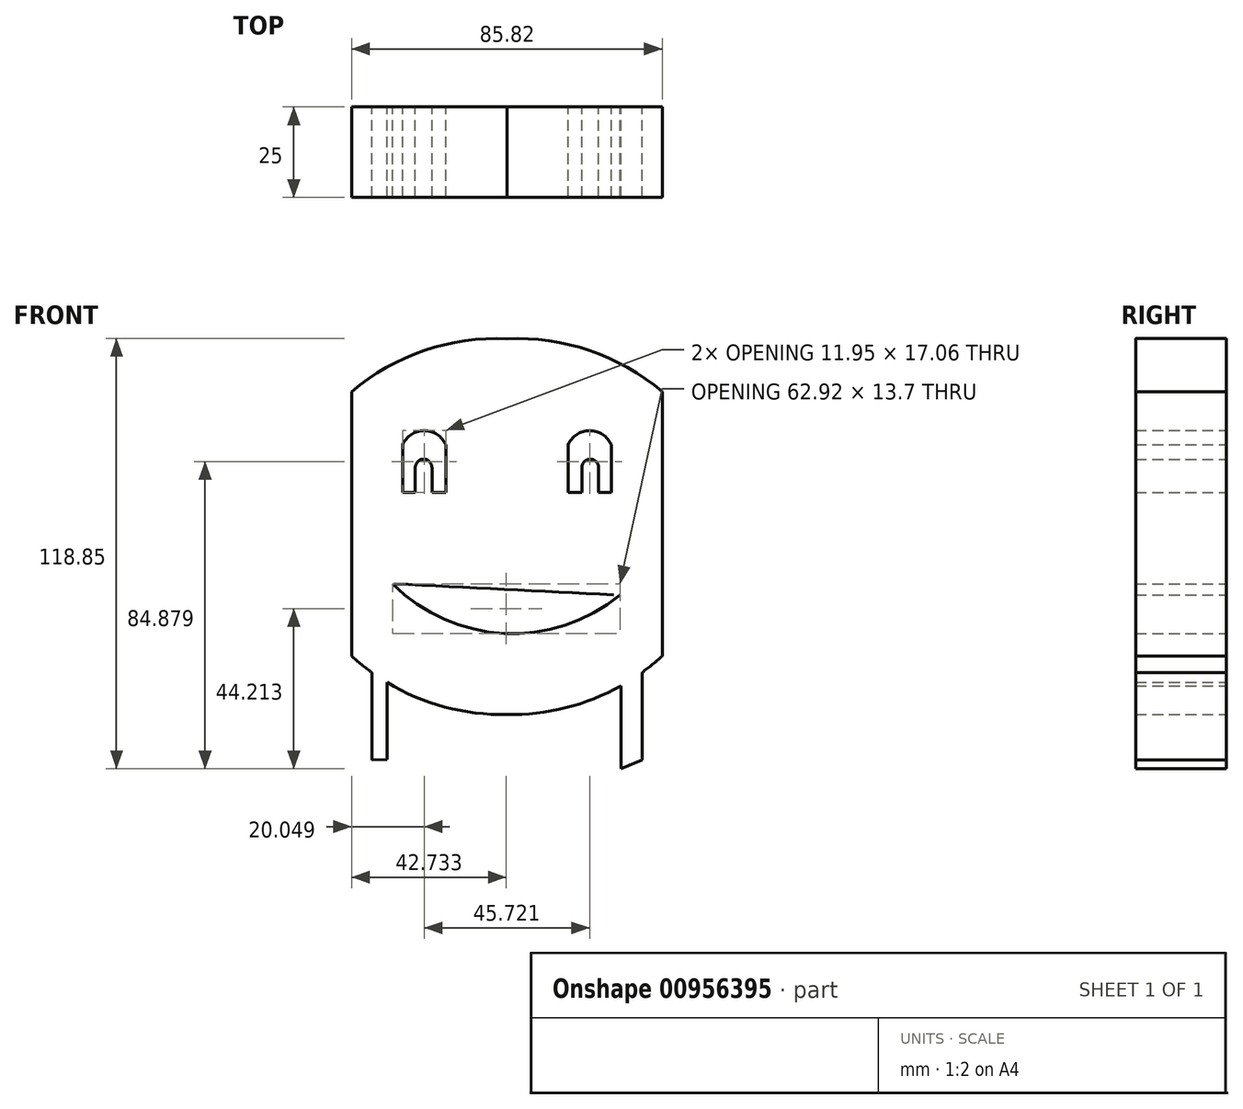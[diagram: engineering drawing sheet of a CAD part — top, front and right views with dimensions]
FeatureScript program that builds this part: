
annotation { "Feature Type Name" : "Feature", "Feature Type Description" : "" }
export const myFeature = defineFeature(function(context is Context, id is Id, definition is map)
    precondition{}
    {
        {
            var Q0;
            Q0=qCreatedBy(makeId("Front.planeOp"),FACE);
            var sketch = newSketch(context, id + "F0", { "sketchPlane" : qUnion([Q0])});
            skPoint(sketch, "E0", {"position": v(0, 0) * mm});
            skLineSegment(sketch, "E1", {"start": v(-37.34, -62.19) * mm, "end": v(-48.84, -66.36) * mm});
            skLineSegment(sketch, "E2", {"start": v(-37.34, -62.19) * mm, "end": v(-37.34, -67.06) * mm});
            skLineSegment(sketch, "E3", {"start": v(-37.34, -62.19) * mm, "end": v(-25.64, -67.08) * mm});
            skLineSegment(sketch, "E4.MirrorCS", {"start": v(37.34, -62.19) * mm, "end": v(25.64, -67.08) * mm});
            skLineSegment(sketch, "E5.MirrorCS", {"start": v(37.34, -62.19) * mm, "end": v(48.84, -66.36) * mm});
            skLineSegment(sketch, "E6.MirrorCS", {"start": v(37.34, -62.19) * mm, "end": v(37.34, -67.06) * mm});
            skArc(sketch, "E7", {"start": v(0, 54.16) * mm, "mid": v(-22.84, 50.9) * mm, "end": v(-42.91, 39.54) * mm});
            skLineSegment(sketch, "E8", {"start": v(-42.91, 39.54) * mm, "end": v(-42.91, -33.53) * mm});
            skArc(sketch, "E9", {"start": v(-42.91, -33.53) * mm, "mid": v(-23, -45.7) * mm, "end": v(0, -49.66) * mm});
            skLineSegment(sketch, "E10", {"start": v(-37.34, -62.19) * mm, "end": v(-37.34, -38.04) * mm});
            skLineSegment(sketch, "E11.MirrorCS", {"start": v(37.34, -62.19) * mm, "end": v(37.34, -38.04) * mm});
            skArc(sketch, "E12.MirrorCS", {"start": v(42.91, -33.53) * mm, "mid": v(23, -45.7) * mm, "end": v(0, -49.66) * mm});
            skLineSegment(sketch, "E13.MirrorCS", {"start": v(42.91, 39.54) * mm, "end": v(42.91, -33.53) * mm});
            skArc(sketch, "E14.MirrorCS", {"start": v(0, 54.16) * mm, "mid": v(22.84, 50.9) * mm, "end": v(42.91, 39.54) * mm});
            skLineSegment(sketch, "E15", {"start": v(-28.84, 11.73) * mm, "end": v(-16.88, 11.73) * mm});
            skLineSegment(sketch, "E16", {"start": v(-28.84, 11.73) * mm, "end": v(-28.84, 24.86) * mm});
            skLineSegment(sketch, "E17", {"start": v(-16.88, 11.73) * mm, "end": v(-16.88, 24.86) * mm});
            skArc(sketch, "E18", {"start": v(-16.88, 24.86) * mm, "mid": v(-22.86, 28.79) * mm, "end": v(-28.84, 24.86) * mm});
            skLineSegment(sketch, "E19.MirrorCS", {"start": v(16.88, 11.73) * mm, "end": v(16.88, 24.86) * mm});
            skArc(sketch, "E20.MirrorCS", {"start": v(16.88, 24.86) * mm, "mid": v(22.86, 28.79) * mm, "end": v(28.84, 24.86) * mm});
            skLineSegment(sketch, "E21.MirrorCS", {"start": v(28.84, 11.73) * mm, "end": v(28.84, 24.86) * mm});
            skLineSegment(sketch, "E22.MirrorCS", {"start": v(28.84, 11.73) * mm, "end": v(16.88, 11.73) * mm});
            skLineSegment(sketch, "E23", {"start": v(-25.3, 11.73) * mm, "end": v(-25.3, 18.59) * mm});
            skLineSegment(sketch, "E24", {"start": v(-20.71, 11.73) * mm, "end": v(-20.71, 18.59) * mm});
            skArc(sketch, "E25", {"start": v(-20.71, 18.59) * mm, "mid": v(-23.01, 20.89) * mm, "end": v(-25.3, 18.59) * mm});
            skLineSegment(sketch, "E26.MirrorCS", {"start": v(20.71, 11.73) * mm, "end": v(20.71, 18.59) * mm});
            skArc(sketch, "E27.MirrorCS", {"start": v(20.71, 18.59) * mm, "mid": v(23.01, 20.89) * mm, "end": v(25.3, 18.59) * mm});
            skLineSegment(sketch, "E28.MirrorCS", {"start": v(25.3, 11.73) * mm, "end": v(25.3, 18.59) * mm});
            skLineSegment(sketch, "E29", {"start": v(-33.12, -40.81) * mm, "end": v(-33.12, -62.07) * mm});
            skLineSegment(sketch, "E30", {"start": v(-33.12, -62.07) * mm, "end": v(-37.34, -62.19) * mm});
            skLineSegment(sketch, "E31", {"start": v(31.52, -41.74) * mm, "end": v(31.52, -64.62) * mm});
            skArc(sketch, "E32", {"start": v(-31.64, -13.55) * mm, "mid": v(-0.78, -27.26) * mm, "end": v(31.29, -16.67) * mm});
            skArc(sketch, "E33", {"start": v(-31.64, -13.55) * mm, "mid": v(-0.18, -15.12) * mm, "end": v(31.29, -16.67) * mm});
            skSolve(sketch);
        }
        {
            var Q0;
            Q0=makeQuery(id+"F0.imprint","IMPRINT",FACE,{"disambiguationData":[TD([[makeQuery(id+"F0.imprint","IMPRINT",EDGE,{"derivedFrom":sQuery(id+"F0.wireOp",EDGE,"E7")}),1.0]])]});
            var Q1;
            {var subQ0=sQuery(id+"F0.wireOp",EDGE,"E23");Q1=makeQuery(id+"F0.imprint","IMPRINT",FACE,{"disambiguationData":[TD([[makeQuery(id+"F0.imprint","IMPRINT",EDGE,{"derivedFrom":subQ0}),-1.0]])]});}
            var Q2;
            {var subQ0=sQuery(id+"F0.wireOp",EDGE,"E26.MirrorCS");Q2=makeQuery(id+"F0.imprint","IMPRINT",FACE,{"disambiguationData":[TD([[makeQuery(id+"F0.imprint","IMPRINT",EDGE,{"derivedFrom":subQ0}),-1.0]])]});}
            var Q3;
            {var subQ0=sQuery(id+"F0.wireOp",EDGE,"E10");Q3=makeQuery(id+"F0.imprint","IMPRINT",FACE,{"disambiguationData":[TD([[makeQuery(id+"F0.imprint","IMPRINT",EDGE,{"derivedFrom":subQ0}),-1.0]])]});}
            var Q4;
            {var subQ0=sQuery(id+"F0.wireOp",EDGE,"E11.MirrorCS");Q4=makeQuery(id+"F0.imprint","IMPRINT",FACE,{"disambiguationData":[TD([[makeQuery(id+"F0.imprint","IMPRINT",EDGE,{"derivedFrom":subQ0}),1.0]])]});}
            extrude(context, id + "F1", {"entities" : qUnion([Q0, Q1, Q2, Q3, Q4]), "depth" : 25 * mm, "offsetDistance" : 25 * mm});
        }
    });
